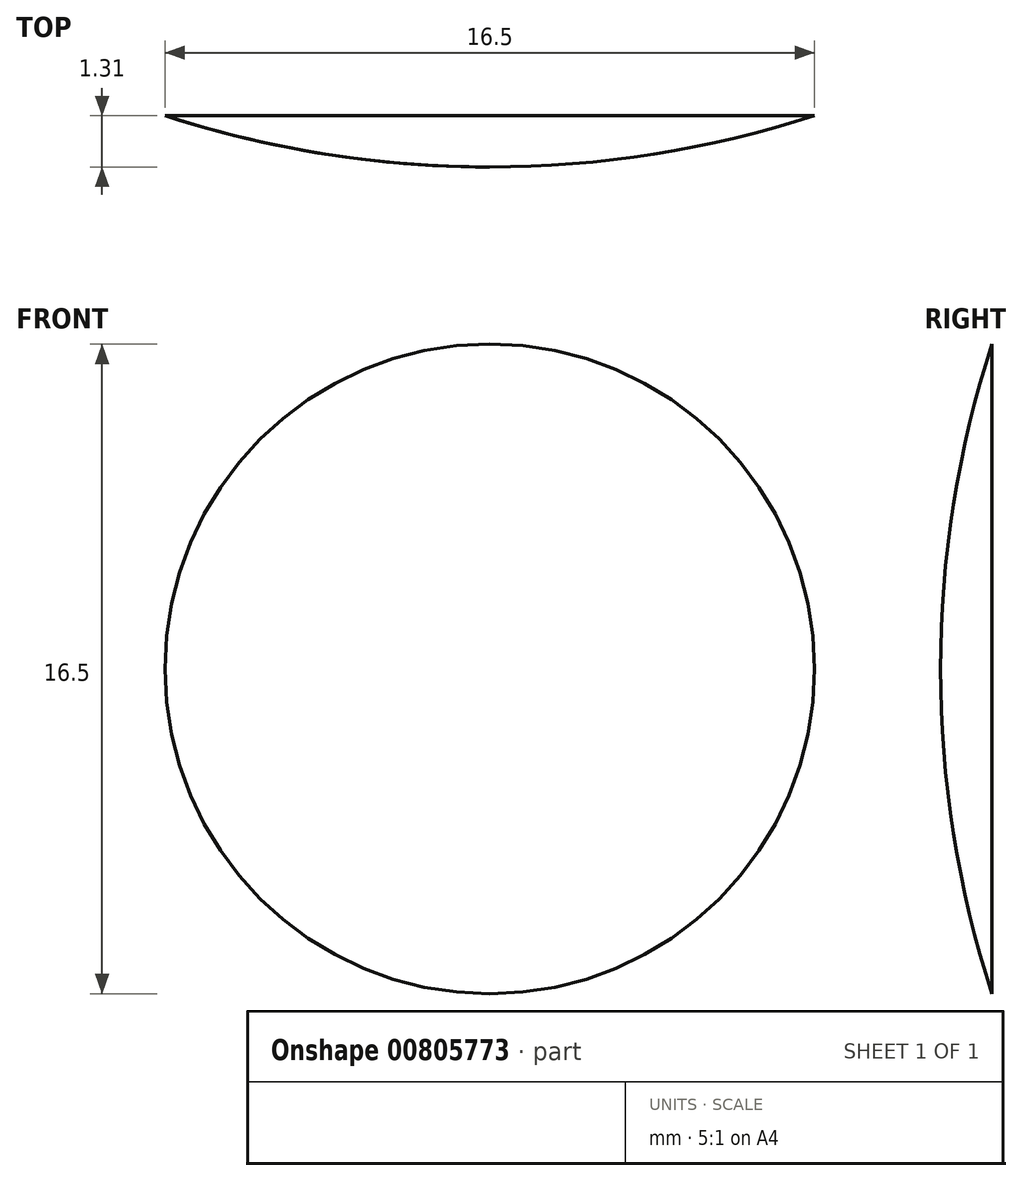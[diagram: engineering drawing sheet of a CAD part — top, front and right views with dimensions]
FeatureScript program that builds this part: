
annotation { "Feature Type Name" : "Feature", "Feature Type Description" : "" }
export const myFeature = defineFeature(function(context is Context, id is Id, definition is map)
    precondition{}
    {
        {
            var Q0;
            Q0=qCreatedBy(makeId("Top.planeOp"),FACE);
            var sketch = newSketch(context, id + "F0", { "sketchPlane" : qUnion([Q0])});
            skLineSegment(sketch, "E0.0", {"start": v(0, 14.04) * mm, "end": v(13.35, 4.34) * mm});
            skLineSegment(sketch, "E0.1", {"start": v(13.35, 4.34) * mm, "end": v(8.25, -11.36) * mm});
            skLineSegment(sketch, "E0.2", {"start": v(8.25, -11.36) * mm, "end": v(-8.25, -11.36) * mm});
            skLineSegment(sketch, "E0.3", {"start": v(-8.25, -11.36) * mm, "end": v(-13.35, 4.34) * mm});
            skLineSegment(sketch, "E0.4", {"start": v(-13.35, 4.34) * mm, "end": v(0, 14.04) * mm});
            skArc(sketch, "E1", {"start": v(13.35, 4.34) * mm, "mid": v(12.05, -3.91) * mm, "end": v(8.25, -11.36) * mm});
            skArc(sketch, "E2", {"start": v(13.35, 4.34) * mm, "mid": v(7.45, 10.25) * mm, "end": v(0, 14.04) * mm});
            skArc(sketch, "E3", {"start": v(-13.35, 4.34) * mm, "mid": v(-7.45, 10.25) * mm, "end": v(0, 14.04) * mm});
            skArc(sketch, "E4", {"start": v(8.25, -11.36) * mm, "mid": v(0, -12.67) * mm, "end": v(-8.25, -11.36) * mm});
            skArc(sketch, "E5", {"start": v(-8.25, -11.36) * mm, "mid": v(-12.05, -3.91) * mm, "end": v(-13.35, 4.34) * mm});
            skLineSegment(sketch, "E6", {"start": v(0, -12.67) * mm, "end": v(0, -11.36) * mm});
            skSolve(sketch);
        }
        {
            var Q0;
            Q0=makeQuery(id+"F0.imprint","IMPRINT",FACE,{"disambiguationData":[TD([[makeQuery(id+"F0.imprint","IMPRINT",EDGE,{"derivedFrom":sQuery(id+"F0.wireOp",EDGE,"E0.0")}),-1.0]])]});
            var Q1;
            Q1=sQuery(id+"F0.wireOp",EDGE,"E5");
            var Q2;
            Q2=sQuery(id+"F0.wireOp",EDGE,"E3");
            var Q3;
            Q3=sQuery(id+"F0.wireOp",EDGE,"E6");
            revolve(context, id + "F1", {"bodyType" : ToolBodyType.SURFACE, "surfaceOperationType" : NewSurfaceOperationType.NEW, "entities" : qUnion([Q0]), "surfaceEntities" : qUnion([Q1, Q2]), "axis" : qUnion([Q3]), "revolveType" : RevolveType.FULL});
        }
        {
            var Q0;
            {var subQ3=sQuery(id+"F0.wireOp",EDGE,"E6");Q0=makeQuery(id+"F0.imprint","IMPRINT",FACE,{"disambiguationData":[TD([[makeQuery(id+"F0.imprint","IMPRINT",EDGE,{"derivedFrom":subQ3}),1.0]])]});}
            var Q1;
            Q1=sQuery(id+"F0.wireOp",EDGE,"E6");
            revolve(context, id + "F2", {"surfaceOperationType" : NewSurfaceOperationType.NEW, "entities" : qUnion([Q0]), "axis" : qUnion([Q1]), "revolveType" : RevolveType.FULL});
        }
    });
